# Revit family: BoelsRental_ScissorLift_Genie_GS3246a
name_source: partatom
category: Site
units: mm (PartAtom-declared; Revit-internal decimal feet)

## family parameters
Always vertical = Yes
Cut with Voids When Loaded = No
OmniClass Number = 23.50.05.14.11
OmniClass Title = Scissors Lifts
Part Type = Normal
Round Connector Dimension = Use Diameter
Shared = No
Work Plane-Based = No

## types (1)
- GS3246
    Assembly Code = E1030100
    AssetType = Movable
    BIMObjectName = BoelsRental_ScissorLift_Genie_GS3246
    BoelsSubgroup = 18055 - Scissor lift 11.7m battery
    ClassificationName = Uniclass2015
    ClassificationValue = Pr_65_80_47_95
    Cost = 0 $
    Description = SCISSOR LIFT, SELF-PROPELLED, PLATFORM WIDTH ≤ 120 CM, ELEC. < 10 M
    DocumentationCertificates = https://www.boels.com
    DocumentationInstallationGuide = https://www.boels.com
    DocumentationLiterature = https://www.boels.com
    DocumentationMaintenance = https://www.boels.com
    DocumentationTechnical = https://www.boels.com
    DurationUnit = Years
    ExpectedLife = 0
    IfcExportAs = IfcTransportElement
    IfcExportType = IfcTransportElementType
    Keynote = X
    Manufacturer = Boels Rental (Genie)
    ManufacturerName = Boels Rental (Genie)
    Material = Steel
    Model = Scissor Lift - GS3246
    ModelNumber = GS3246
    ModelReference = Scissor Lift
    NBSDescription = Vertical lifting platforms
    NBSObjectName = Boels Rental - Vertical lifting platforms
    NBSReference = 90-80-65/350
    NominalDepth = 1160 mm
    NominalHeight = 2390 mm
    NominalLength = 2440 mm
    ProductPageLink = https://www.boels.com
    ProductionYear = 2022
    Size = 1160mm x 2390mm x 2440mm
    Type Comments = Scissor Lift - GS3246
    TypeName = Scissor Lift - GS3246
    URL = https://www.boels.com
    WarrantyDurationLabor = 0
    WarrantyDurationParts = 0
    WarrantyDurationUnit = Years
    WarrantyGuarantorLabor = https://www.boels.com
    WarrantyGuarantorParts = https://www.boels.com
    _BSBibleVersion = 16
    _BimSpecGuid = 0
    _CurrentRevision = 1
    _DistributedBy = https://www.boels.com
    _ObjectUserGuide = https://www.boels.com

## geometry (parser evidence)
native form markers: Sweep x30
no freeform markers — native parametric forms only
